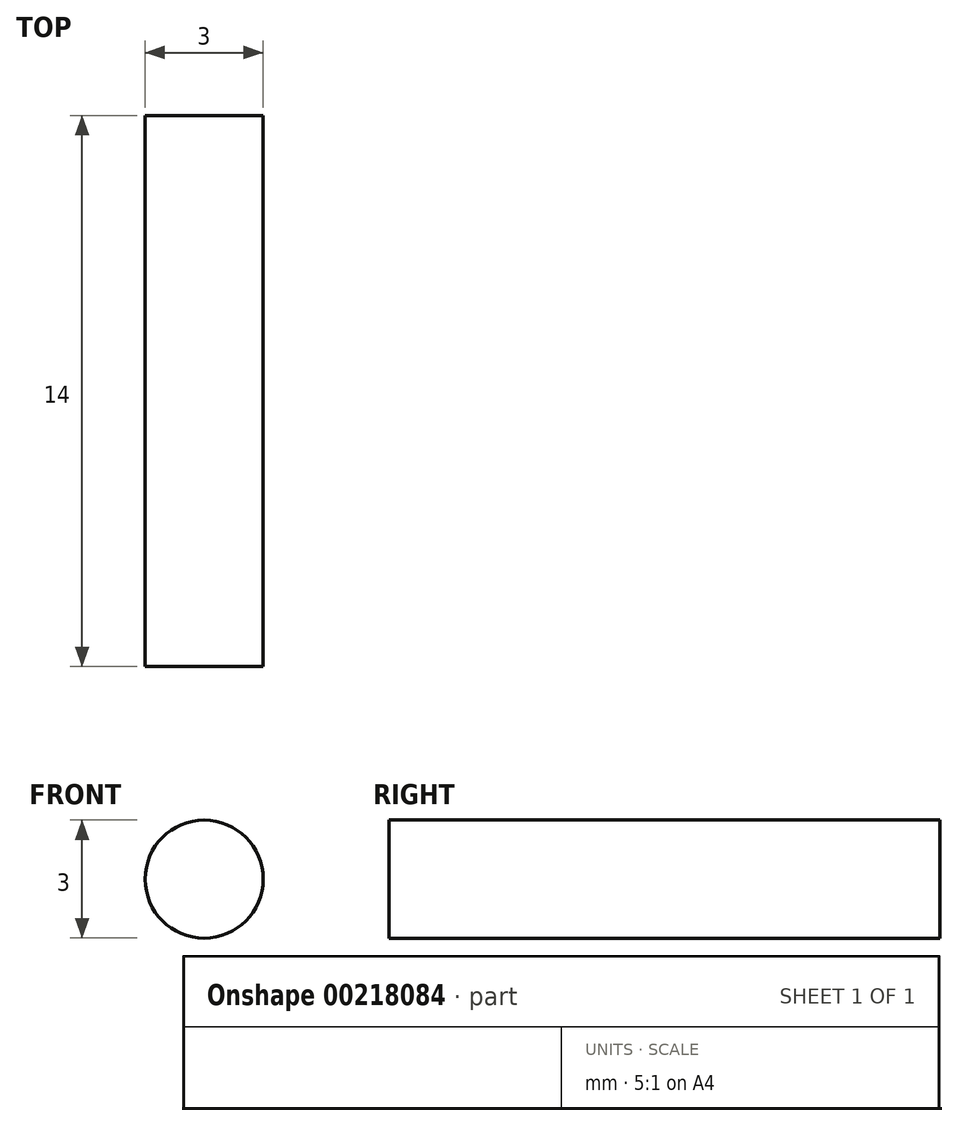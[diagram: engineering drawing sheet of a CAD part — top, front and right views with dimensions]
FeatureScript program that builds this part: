
annotation { "Feature Type Name" : "Feature", "Feature Type Description" : "" }
export const myFeature = defineFeature(function(context is Context, id is Id, definition is map)
    precondition{}
    {
        {
            var Q0;
            Q0=qCreatedBy(makeId("Front.planeOp"),FACE);
            var sketch = newSketch(context, id + "F0", { "sketchPlane" : qUnion([Q0])});
            skCircle(sketch, "E0", {"center": v(18.68, 12.5) * mm, "radius": 1.5 * mm});
            skSolve(sketch);
        }
        {
            var Q0;
            Q0=makeQuery(id+"F0.imprint","IMPRINT",FACE,{"disambiguationData":[TD([[makeQuery(id+"F0.imprint","IMPRINT",EDGE,{"derivedFrom":sQuery(id+"F0.wireOp",EDGE,"E0")}),1.0]])]});
            extrude(context, id + "F1", {"entities" : qUnion([Q0]), "depth" : 14 * mm});
        }
    });
